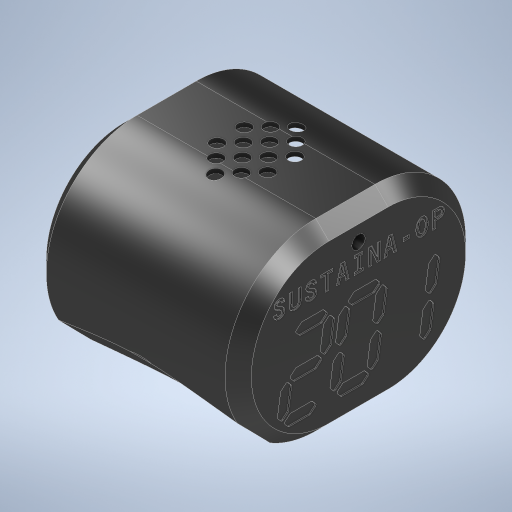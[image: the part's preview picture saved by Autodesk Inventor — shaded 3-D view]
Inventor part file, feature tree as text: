
AUTODESK INVENTOR PART (.ipt)
format: ipt  version: 2024.2 (Build 282272000, 272)  size: 1,420,800 bytes
history: native  units: mm
features: sketch x4, extrude x4, other x2, revolve x1, mirror x1, hole x1, pattern_circular x1, projected_geometry x1
ambient origin geometry x8: Origin, YZ Plane, XZ Plane, XY Plane, X Axis, Y Axis, Z Axis, Center Point
bodies: Solid1 (feature_tree)
feature tree (15):
  other  "HeadSideFrame_.ipt"
  sketch  "Sketch2"  dims[d4=0.25mm d5=0.25mm]
  extrude  "Extrusion1"  Depth=0.25mm
  revolve  "Revolution1"  [1 undecoded]
  extrude  "Extrusion2"  Depth=5.0mm TaperAngle=45.0deg
  extrude  "Extrusion3"  Depth=0.5mm
  mirror  "Mirror1"
  sketch  "Sketch3"  dims[d6=39.0mm d7=0.0mm d8=5.0mm d9=2.0mm d10=45.0deg]
  extrude  "Extrusion4"  Depth=0.5mm
  hole  "Hole1"  [1 undecoded]
  other  "Work Axis1"
  pattern_circular  "Circular Pattern1"  [2 undecoded]
  sketch  "Sketch1"  dims[d0=10.0mm d1=0.25mm]
  projected_geometry  "Projected Loop1"
  sketch  "Sketch4"  dims[d11=180.0deg d13=20.0mm d15=20.0mm d17=30.0mm d19=10.0mm d21=20.0mm d23=20.0mm d24=1.25mm d25=4.166667mm d26=4.166667mm d27=12.5mm d28=12.5mm d29=0.625mm d30=14.14689mm d31=14.14689mm d32=14.14689mm d33=20.0mm d34=20.0mm d35=10.0mm d36=22.5mm d37=1.396263mm d39=0.5mm d40=0.0mm d41=25.0mm d42=33.0mm d43=0.0mm d44=40.0mm d45=28.3mm d48=5.0mm d49=0.0mm d50=2.0mm d51=2.0mm d52=0.25mm d53=2.0mm d54=20.0mm d55=360.0deg d57=2.5mm d58=6.0mm d59=5.0mm d60=3.5mm d61=90.0deg d62=8.0mm d63=0.0mm d64=5.0mm]
note: 4 required parameter values undecoded (feature->parameter linkage not recoverable at this tier; creation-order binding heuristic only, values carry confidence <= 0.55)